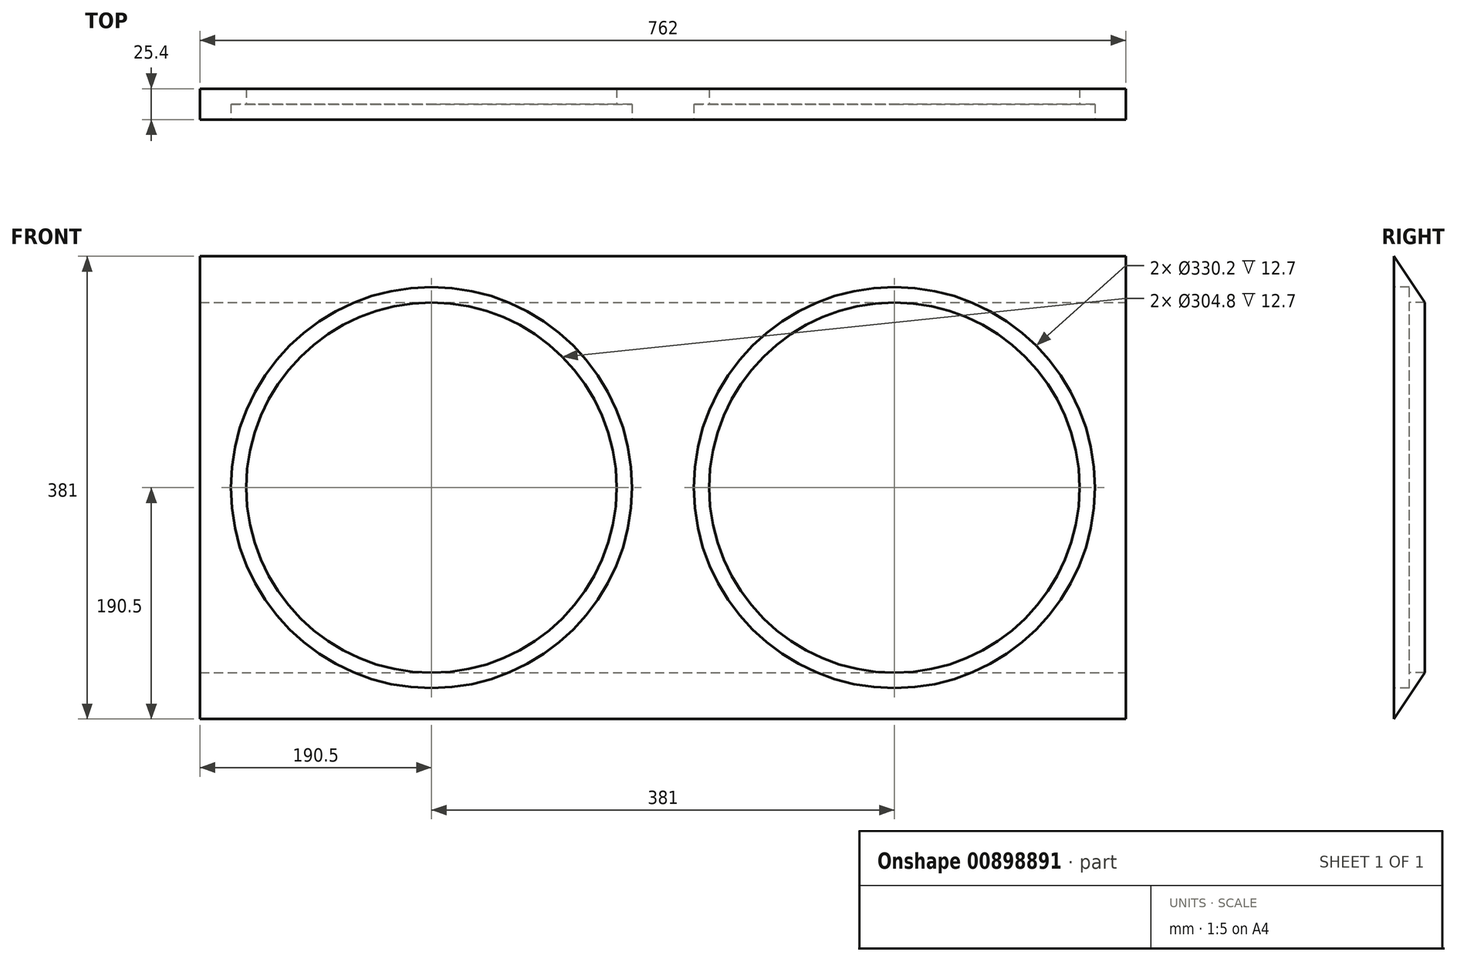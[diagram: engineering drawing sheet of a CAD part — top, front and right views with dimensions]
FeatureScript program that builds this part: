
annotation { "Feature Type Name" : "Feature", "Feature Type Description" : "" }
export const myFeature = defineFeature(function(context is Context, id is Id, definition is map)
    precondition{}
    {
        {
            var Q0;
            Q0=qCreatedBy(makeId("Front.planeOp"),FACE);
            var sketch = newSketch(context, id + "F0", { "sketchPlane" : qUnion([Q0])});
            skLineSegment(sketch, "E0.bottom", {"start": v(-381, 190.5) * mm, "end": v(381, 190.5) * mm});
            skLineSegment(sketch, "E0.top", {"start": v(-381, -190.5) * mm, "end": v(381, -190.5) * mm});
            skLineSegment(sketch, "E0.left", {"start": v(-381, 190.5) * mm, "end": v(-381, -190.5) * mm});
            skLineSegment(sketch, "E0.right", {"start": v(381, 190.5) * mm, "end": v(381, -190.5) * mm});
            skSolve(sketch);
        }
        {
            var Q0;
            Q0=makeQuery(id+"F0.imprint","IMPRINT",FACE,{"disambiguationData":[TD([[makeQuery(id+"F0.imprint","IMPRINT",EDGE,{"derivedFrom":sQuery(id+"F0.wireOp",EDGE,"E0.bottom")}),-1.0]])]});
            extrude(context, id + "F1", {"entities" : qUnion([Q0]), "oppositeDirection" : true, "depth" : 25.4 * mm, "offsetDistance" : 25.4 * mm});
        }
        {
            var Q0;
            Q0=makeQuery(id+"F1.opExtrude","CAP_FACE",FACE,{"disambiguationData":[OSD([sQuery(id+"F0.wireOp",EDGE,"E0.bottom"),sQuery(id+"F0.wireOp",EDGE,"E0.top"),sQuery(id+"F0.wireOp",EDGE,"E0.left"),sQuery(id+"F0.wireOp",EDGE,"E0.right")])],"isStart":true});
            var sketch = newSketch(context, id + "F2", { "sketchPlane" : qUnion([Q0])});
            skCircle(sketch, "E1", {"center": v(-190.5, 0) * mm, "radius": 165.1 * mm});
            skCircle(sketch, "E2", {"center": v(190.5, 0) * mm, "radius": 165.1 * mm});
            skSolve(sketch);
        }
        {
            var Q0;
            Q0 = qSketchRegion(id + "F2", true);
            extrude(context, id + "F3", {"entities" : qUnion([Q0]), "operationType" : NewBodyOperationType.REMOVE, "oppositeDirection" : true, "depth" : 12.7 * mm, "offsetDistance" : 25.4 * mm});
        }
        {
            var Q0;
            Q0=makeQuery(id+"F3.boolean.opBoolean","COPY",FACE,{"derivedFrom":makeQuery(id+"F3.opExtrude","CAP_FACE",FACE,{"disambiguationData":[OSD([sQuery(id+"F2.wireOp",EDGE,"E1")])],"isStart":false})});
            var sketch = newSketch(context, id + "F4", { "sketchPlane" : qUnion([Q0])});
            skCircle(sketch, "E3", {"center": v(-190.5, 0) * mm, "radius": 152.4 * mm});
            skCircle(sketch, "E4", {"center": v(190.5, 0) * mm, "radius": 152.4 * mm});
            skSolve(sketch);
        }
        {
            var Q0;
            Q0 = qSketchRegion(id + "F4", true);
            extrude(context, id + "F5", {"entities" : qUnion([Q0]), "operationType" : NewBodyOperationType.REMOVE, "oppositeDirection" : true, "depth" : 25.4 * mm, "offsetDistance" : 25.4 * mm});
        }
        {
            var Q0;
            Q0=makeQuery(id+"F1.opExtrude","SWEPT_FACE",FACE,{"disambiguationData":[OSD([sQuery(id+"F0.wireOp",EDGE,"E0.right")])]});
            var sketch = newSketch(context, id + "F6", { "sketchPlane" : qUnion([Q0])});
            skLineSegment(sketch, "E5.left", {"start": v(25.4, -190.5) * mm, "end": v(25.4, -152.4) * mm});
            skLineSegment(sketch, "E6", {"start": v(25.4, -190.5) * mm, "end": v(0, -190.5) * mm});
            skLineSegment(sketch, "E7", {"start": v(0, -190.5) * mm, "end": v(25.4, -152.4) * mm});
            skLineSegment(sketch, "E8.bottom", {"start": v(0, 190.5) * mm, "end": v(25.4, 190.5) * mm});
            skLineSegment(sketch, "E8.right", {"start": v(25.4, 190.5) * mm, "end": v(25.4, 152.4) * mm});
            skLineSegment(sketch, "E9", {"start": v(0, 190.5) * mm, "end": v(25.4, 152.4) * mm});
            skSolve(sketch);
        }
        {
            var Q0;
            Q0 = qSketchRegion(id + "F6", true);
            extrude(context, id + "F7", {"entities" : qUnion([Q0]), "operationType" : NewBodyOperationType.REMOVE, "oppositeDirection" : true, "depth" : 762 * mm, "offsetDistance" : 25.4 * mm});
        }
    });
